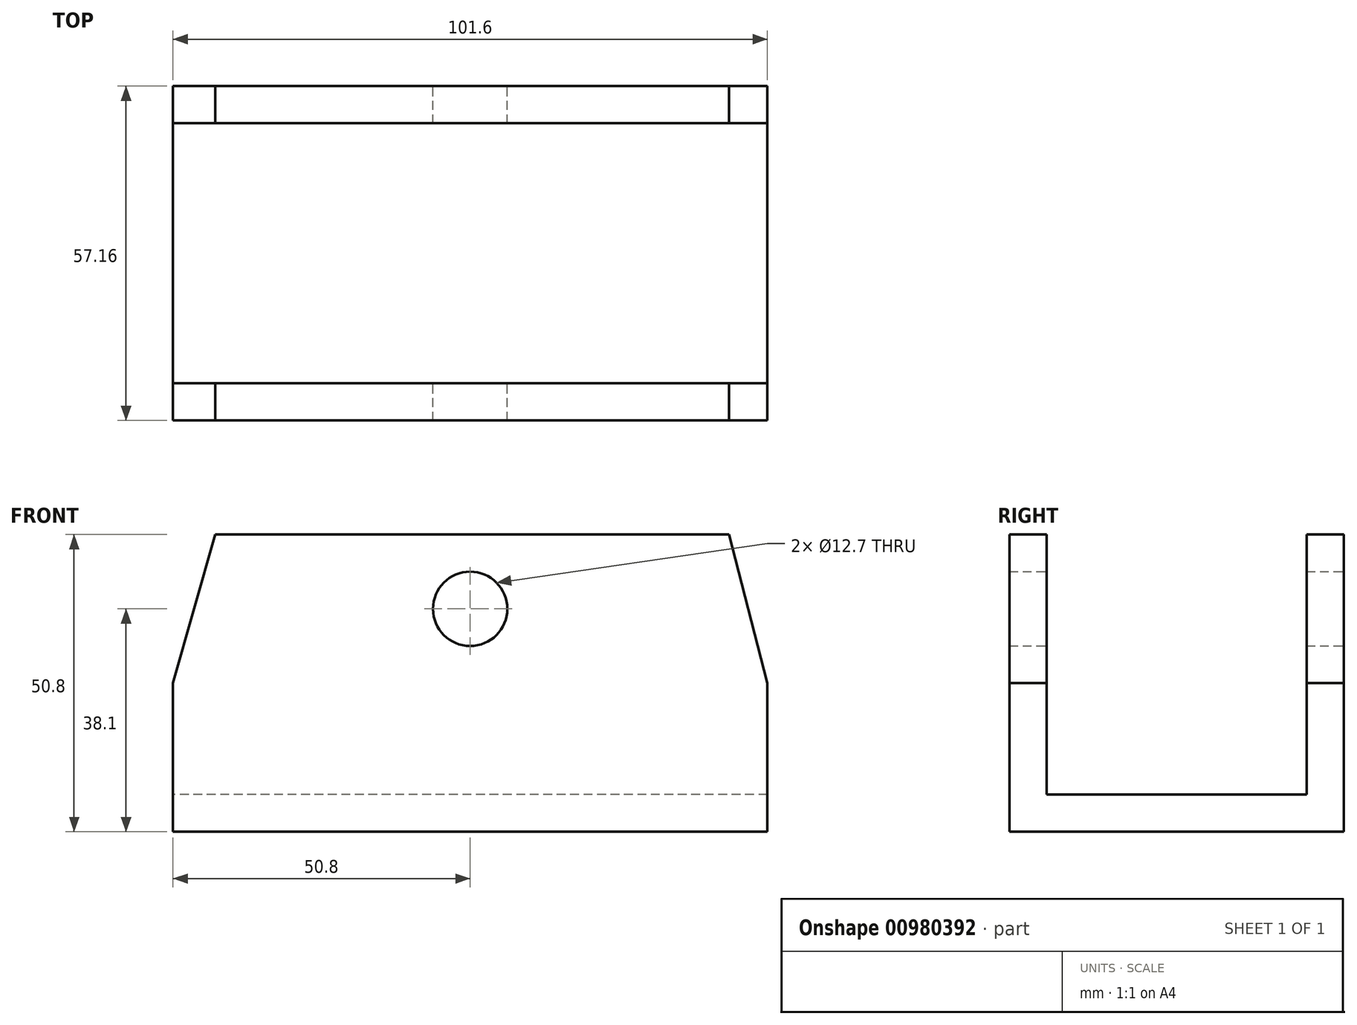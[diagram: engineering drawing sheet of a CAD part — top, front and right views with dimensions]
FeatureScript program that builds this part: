
annotation { "Feature Type Name" : "Feature", "Feature Type Description" : "" }
export const myFeature = defineFeature(function(context is Context, id is Id, definition is map)
    precondition{}
    {
        {
            var Q0;
            Q0=qCreatedBy(makeId("Front.planeOp"),FACE);
            var sketch = newSketch(context, id + "F0", { "sketchPlane" : qUnion([Q0])});
            skLineSegment(sketch, "E0", {"start": v(-50.8, 0) * mm, "end": v(50.8, 0) * mm});
            skLineSegment(sketch, "E1", {"start": v(50.8, 0) * mm, "end": v(50.8, 25.4) * mm});
            skLineSegment(sketch, "E2", {"start": v(50.8, 25.4) * mm, "end": v(44.25, 50.8) * mm});
            skLineSegment(sketch, "E3", {"start": v(44.25, 50.8) * mm, "end": v(-43.55, 50.8) * mm});
            skLineSegment(sketch, "E4", {"start": v(-43.55, 50.8) * mm, "end": v(-50.8, 25.4) * mm});
            skLineSegment(sketch, "E5", {"start": v(-50.8, 25.4) * mm, "end": v(-50.8, 0) * mm});
            skSolve(sketch);
        }
        {
            var Q0;
            Q0 = qSketchRegion(id + "F0", true);
            extrude(context, id + "F1", {"entities" : qUnion([Q0]), "endBound" : BoundingType.SYMMETRIC, "depth" : 57.15 * mm, "offsetDistance" : 25.4 * mm});
        }
        {
            var Q0;
            Q0=makeQuery(id+"F1.opExtrude","SWEPT_FACE",FACE,{"disambiguationData":[OSD([sQuery(id+"F0.wireOp",EDGE,"E5")])]});
            var sketch = newSketch(context, id + "F2", { "sketchPlane" : qUnion([Q0])});
            skLineSegment(sketch, "E6.bottom", {"start": v(-22.23, 6.35) * mm, "end": v(22.23, 6.35) * mm});
            skLineSegment(sketch, "E6.top", {"start": v(-22.23, 50.8) * mm, "end": v(22.22, 50.8) * mm});
            skLineSegment(sketch, "E6.left", {"start": v(-22.23, 6.35) * mm, "end": v(-22.23, 50.8) * mm});
            skLineSegment(sketch, "E6.right", {"start": v(22.23, 6.35) * mm, "end": v(22.22, 50.8) * mm});
            skSolve(sketch);
        }
        {
            var Q0;
            Q0 = qSketchRegion(id + "F2", true);
            extrude(context, id + "F3", {"entities" : qUnion([Q0]), "operationType" : NewBodyOperationType.REMOVE, "oppositeDirection" : true, "depth" : 127 * mm, "offsetDistance" : 25.4 * mm});
        }
        {
            var Q0;
            Q0=makeQuery(id+"F1.opExtrude","CAP_FACE",FACE,{"disambiguationData":[OSD([sQuery(id+"F0.wireOp",EDGE,"E0"),sQuery(id+"F0.wireOp",EDGE,"E1"),sQuery(id+"F0.wireOp",EDGE,"E2"),sQuery(id+"F0.wireOp",EDGE,"E3"),sQuery(id+"F0.wireOp",EDGE,"E4"),sQuery(id+"F0.wireOp",EDGE,"E5")])],"isStart":true});
            var sketch = newSketch(context, id + "F4", { "sketchPlane" : qUnion([Q0])});
            skCircle(sketch, "E7", {"center": v(0, 38.1) * mm, "radius": 6.35 * mm});
            skSolve(sketch);
        }
        {
            var Q0;
            Q0 = qSketchRegion(id + "F4", true);
            extrude(context, id + "F5", {"entities" : qUnion([Q0]), "operationType" : NewBodyOperationType.REMOVE, "endBound" : BoundingType.THROUGH_ALL, "oppositeDirection" : true, "depth" : 25.4 * mm, "offsetDistance" : 25.4 * mm});
        }
    });
